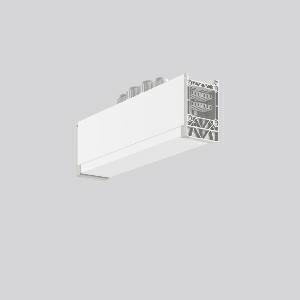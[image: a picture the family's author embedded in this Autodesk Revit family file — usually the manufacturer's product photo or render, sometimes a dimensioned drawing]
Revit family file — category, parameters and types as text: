
# Revit family: linedo_mitteleinspeisung_14pol_b_b_982698_012_1_6254
name_source: partatom
category: Lighting Fixtures
units: mm (PartAtom-declared; Revit-internal decimal feet)

## family parameters
Cut with Voids When Loaded = No
Host = Face
Light Source = No
Part Type = Normal
Room Calculation Point = No
Round Connector Dimension = Use Diameter
Shared = No

## types (1)
- LINEDO_Mitteleinspeisung_14pol_B_B
    Apparent Load = 0 VA
    Default Elevation = 1800 mm
    Description = Series: LINEDO
Middle power feed, 14-pole, connection socket / socket. Housing: extruded aluminium profile, powder-coated. Cover made of plastic, surface like housing. LINEDO plug system, plastic, light grey. 4 cable glands (2 x M20 and 2 x M25). Cable glands on top. Easy connection for rigid or flexible wires. Especially for use with continuous line modules with high opal diffuser.
Colour: white
Length: 312 mm
Width: 58 mm
Height: 91 mm
Weight: 900 g
    Height = 91 mm
    Lamp = 0 x
    Length = 312 mm
    Luminous efficacy = 0 lm/W
    Manufacturer = RZB
    ModVariant = No
    Model = 982698.012.1
    Mounting Place = Ceiling
    Mounting Type = Surface mounted
    Number of Poles = 1
    OnlyDefault = Yes
    Power Factor = 1
    Product Name = LINEDO_Mitteleinspeisung_14pol_B_B
    Product group = Surface mounted continuous line luminaire system
    ProductGroupID = 310
    Protection Class = Protection class I
    Protection Degree = Degree of protection
    RLX_Detail_Level = 1
    RLX_Emergency_Light_Flux = 0 lm
    RLX_Emergency_Type = 0
    RLX_Emergency_Type_DB = No
    RlxData = <blob elided: 22169 chars, md5=f7dd06ca>
    Standby Power = 0 W
    System Light Flux = 0 lm
    System Power = 0 W
    Type Comments = Product without accessories
    Type Image = 982698.012.1.jpg
    URL = http://relux.com
    VarID = ---
    Voltage = 0 V
    Weight = 0.00 kg
    Width = 58 mm

## geometry (parser evidence)
native form markers: Blend x4, Sweep x11
no freeform markers — native parametric forms only
